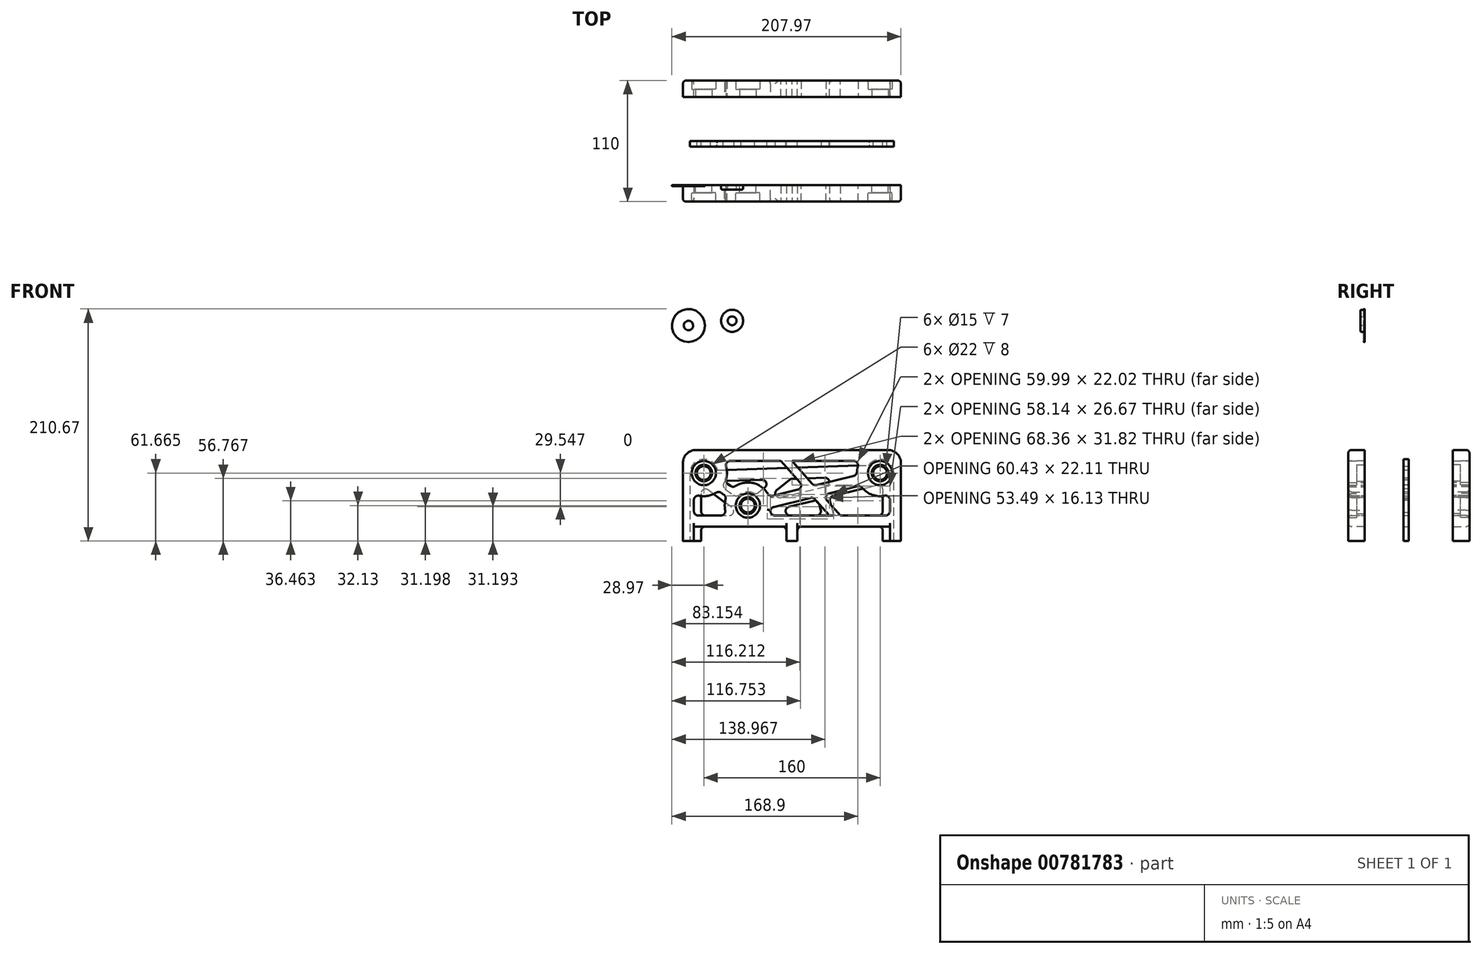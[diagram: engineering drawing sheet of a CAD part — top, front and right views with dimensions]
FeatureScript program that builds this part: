
annotation { "Feature Type Name" : "Feature", "Feature Type Description" : "" }
export const myFeature = defineFeature(function(context is Context, id is Id, definition is map)
    precondition{}
    {
        {
            var Q0;
            Q0=qCreatedBy(makeId("Front.planeOp"),FACE);
            var sketch = newSketch(context, id + "F0", { "sketchPlane" : qUnion([Q0])});
            skCircle(sketch, "E0", {"center": v(0, 0) * mm, "radius": 100 * mm, "construction": true});
            skLineSegment(sketch, "E1", {"start": v(-89.15, -115) * mm, "end": v(130.91, -115) * mm, "construction": true});
            skCircle(sketch, "E2", {"center": v(-80, -66.45) * mm, "radius": 11 * mm});
            skCircle(sketch, "E3", {"center": v(-40, -96) * mm, "radius": 11 * mm});
            skCircle(sketch, "E4", {"center": v(80, -66.45) * mm, "radius": 11 * mm});
            skCircle(sketch, "E5", {"center": v(8.23, -33.43) * mm, "radius": 75 * mm, "construction": true});
            skLineSegment(sketch, "E6", {"start": v(-99, -45.45) * mm, "end": v(-99, -115) * mm});
            skLineSegment(sketch, "E7", {"start": v(-99, -115) * mm, "end": v(99, -115) * mm});
            skLineSegment(sketch, "E8", {"start": v(99, -115) * mm, "end": v(99, -45.45) * mm});
            skCircle(sketch, "E9", {"center": v(-80, -66.45) * mm, "radius": 4 * mm, "construction": true});
            skCircle(sketch, "E10", {"center": v(-40, -96) * mm, "radius": 4 * mm, "construction": true});
            skCircle(sketch, "E11", {"center": v(80, -66.45) * mm, "radius": 4 * mm, "construction": true});
            skLineSegment(sketch, "E12", {"start": v(-99, -45.45) * mm, "end": v(99, -45.45) * mm});
            skCircle(sketch, "E13", {"center": v(-80, -66.45) * mm, "radius": 7.5 * mm});
            skCircle(sketch, "E14", {"center": v(-40, -96) * mm, "radius": 7.5 * mm});
            skCircle(sketch, "E15", {"center": v(80, -66.45) * mm, "radius": 7.5 * mm});
            skSolve(sketch);
        }
        {
            var Q0;
            Q0=makeQuery(id+"F0.imprint","IMPRINT",FACE,{"disambiguationData":[TD([[makeQuery(id+"F0.imprint","IMPRINT",EDGE,{"derivedFrom":sQuery(id+"F0.wireOp",EDGE,"E2")}),-1.0]])]});
            var Q1;
            Q1=makeQuery(id+"F0.imprint","IMPRINT",FACE,{"disambiguationData":[TD([[makeQuery(id+"F0.imprint","IMPRINT",EDGE,{"derivedFrom":sQuery(id+"F0.wireOp",EDGE,"E2")}),1.0]])]});
            var Q2;
            Q2=makeQuery(id+"F0.imprint","IMPRINT",FACE,{"disambiguationData":[TD([[makeQuery(id+"F0.imprint","IMPRINT",EDGE,{"derivedFrom":sQuery(id+"F0.wireOp",EDGE,"E3")}),1.0]])]});
            var Q3;
            Q3=makeQuery(id+"F0.imprint","IMPRINT",FACE,{"disambiguationData":[TD([[makeQuery(id+"F0.imprint","IMPRINT",EDGE,{"derivedFrom":sQuery(id+"F0.wireOp",EDGE,"E4")}),1.0]])]});
            extrude(context, id + "F1", {"entities" : qUnion([Q0, Q1, Q2, Q3]), "depth" : 15 * mm, "offsetDistance" : 25 * mm});
        }
        {
            var Q0;
            Q0=makeQuery(id+"F0.imprint","IMPRINT",FACE,{"disambiguationData":[TD([[makeQuery(id+"F0.imprint","IMPRINT",EDGE,{"derivedFrom":sQuery(id+"F0.wireOp",EDGE,"E2")}),1.0]])]});
            var Q1;
            Q1=makeQuery(id+"F0.imprint","IMPRINT",FACE,{"disambiguationData":[TD([[makeQuery(id+"F0.imprint","IMPRINT",EDGE,{"derivedFrom":sQuery(id+"F0.wireOp",EDGE,"E3")}),1.0]])]});
            var Q2;
            Q2=makeQuery(id+"F0.imprint","IMPRINT",FACE,{"disambiguationData":[TD([[makeQuery(id+"F0.imprint","IMPRINT",EDGE,{"derivedFrom":sQuery(id+"F0.wireOp",EDGE,"E4")}),1.0]])]});
            var Q3;
            Q3=makeQuery(id+"F1.opExtrude","CAP_FACE",FACE,{"disambiguationData":[OSD([sQuery(id+"F0.wireOp",EDGE,"E6"),sQuery(id+"F0.wireOp",EDGE,"E7"),sQuery(id+"F0.wireOp",EDGE,"E8"),sQuery(id+"F0.wireOp",EDGE,"E12"),sQuery(id+"F0.wireOp",EDGE,"E13"),sQuery(id+"F0.wireOp",EDGE,"E14"),sQuery(id+"F0.wireOp",EDGE,"E15")])],"isStart":false});
            extrude(context, id + "F2", {"entities" : qUnion([Q0, Q1, Q2]), "operationType" : NewBodyOperationType.REMOVE, "endBound" : BoundingType.UP_TO_SURFACE, "depth" : 25 * mm, "endBoundEntityFace" : qUnion([Q3]), "offsetDistance" : 25 * mm, "hasSecondDirection" : true, "secondDirectionOppositeDirection" : false, "secondDirectionDepth" : 7 * mm});
        }
        {
            var Q0;
            Q0=makeQuery(id+"F1.opExtrude","CAP_FACE",FACE,{"disambiguationData":[OSD([sQuery(id+"F0.wireOp",EDGE,"E2"),sQuery(id+"F0.wireOp",EDGE,"E3"),sQuery(id+"F0.wireOp",EDGE,"E4"),sQuery(id+"F0.wireOp",EDGE,"E6"),sQuery(id+"F0.wireOp",EDGE,"E7"),sQuery(id+"F0.wireOp",EDGE,"E8"),sQuery(id+"F0.wireOp",EDGE,"md6mKMxj-XIqy-UovL-ZTLQ-MiWI4Y2psHtO"),sQuery(id+"F0.wireOp",EDGE,"icawwdYT-1uhy-4dwY-ULv6-UgLao4UIgMBT"),sQuery(id+"F0.wireOp",EDGE,"7s30I3XL-TyKG-oTAD-cgkG-Kr0AbNeQ8WuT")])],"isStart":false});
            shell(context, id + "F3", {"entities" : qUnion([Q0]), "thickness" : 10 * mm});
        }
        {
            var Q0;
            Q0=makeQuery(id+"F3.opShell","OFFSET_FACE",FACE,{"disambiguationData":[OSD([sQuery(id+"F0.wireOp",EDGE,"E6"),sQuery(id+"F0.wireOp",EDGE,"E7"),sQuery(id+"F0.wireOp",EDGE,"E8"),sQuery(id+"F0.wireOp",EDGE,"E12"),sQuery(id+"F0.wireOp",EDGE,"E13"),sQuery(id+"F0.wireOp",EDGE,"E14"),sQuery(id+"F0.wireOp",EDGE,"E15")])]});
            extrude(context, id + "F4", {"entities" : qUnion([Q0]), "operationType" : NewBodyOperationType.REMOVE, "oppositeDirection" : true, "depth" : 25 * mm, "offsetDistance" : 25 * mm, "symmetric" : true});
        }
        {
            var Q0;
            Q0=makeQuery(id+"F1.opExtrude","CAP_FACE",FACE,{"disambiguationData":[OSD([sQuery(id+"F0.wireOp",EDGE,"E6"),sQuery(id+"F0.wireOp",EDGE,"E7"),sQuery(id+"F0.wireOp",EDGE,"E8"),sQuery(id+"F0.wireOp",EDGE,"E12"),sQuery(id+"F0.wireOp",EDGE,"E13"),sQuery(id+"F0.wireOp",EDGE,"E14"),sQuery(id+"F0.wireOp",EDGE,"E15")])],"isStart":false});
            var sketch = newSketch(context, id + "F5", { "sketchPlane" : qUnion([Q0])});
            skCircle(sketch, "E16.0", {"center": v(-80, -66.45) * mm, "radius": 7.5 * mm, "construction": true});
            skCircle(sketch, "E17.0", {"center": v(-40, -96) * mm, "radius": 7.5 * mm, "construction": true});
            skCircle(sketch, "E18.0", {"center": v(80, -66.45) * mm, "radius": 7.5 * mm, "construction": true});
            skLineSegment(sketch, "E19", {"start": v(-78.47, -73.8) * mm, "end": v(-47.47, -96.7) * mm});
            skLineSegment(sketch, "E20", {"start": v(-81.53, -59.1) * mm, "end": v(-32.53, -95.3) * mm});
            skCircle(sketch, "E21.0", {"center": v(-80, -66.45) * mm, "radius": 11 * mm});
            skCircle(sketch, "E22.0", {"center": v(-40, -96) * mm, "radius": 11 * mm});
            skCircle(sketch, "E23.0", {"center": v(80, -66.45) * mm, "radius": 11 * mm});
            skLineSegment(sketch, "E24", {"start": v(-32.72, -94.2) * mm, "end": v(72.72, -68.25) * mm, "construction": true});
            skLineSegment(sketch, "E25", {"start": v(-30.55, -90.38) * mm, "end": v(69.02, -65.86) * mm});
            skLineSegment(sketch, "E26", {"start": v(73.23, -75.12) * mm, "end": v(-29.98, -100.54) * mm});
            skLineSegment(sketch, "E27", {"start": v(0, -55.45) * mm, "end": v(43.99, -105) * mm});
            skLineSegment(sketch, "E28", {"start": v(33.99, -105) * mm, "end": v(-10, -55.45) * mm});
            skLineSegment(sketch, "E29", {"start": v(-80, -66.45) * mm, "end": v(-40, -96) * mm, "construction": true});
            skSolve(sketch);
        }
        {
            var Q0;
            {var subQ0=sQuery(id+"F5.wireOp",EDGE,"E25");var subQ1=sQuery(id+"F0.wireOp",EDGE,"E15");var subQ2=sQuery(id+"F0.wireOp",EDGE,"E14");var subQ3=sQuery(id+"F0.wireOp",EDGE,"E13");var subQ4=sQuery(id+"F0.wireOp",EDGE,"E12");var subQ5=sQuery(id+"F0.wireOp",EDGE,"E8");var subQ6=sQuery(id+"F0.wireOp",EDGE,"E7");var subQ7=sQuery(id+"F0.wireOp",EDGE,"E6");var subQ8=makeQuery(id+"F3.opShell","OFFSET_EDGE",EDGE,{"disambiguationData":[OSD([sQuery(id+"F0.wireOp",EDGE,"E3"),subQ7,subQ6,subQ5,subQ4,subQ3,subQ2,subQ1])]});var subQ9=makeQuery(id+"F5.imprint","INTERSECT",VERTEX,{"derivedFrom":[subQ8,subQ0]});Q0=makeQuery(id+"F5.imprint","IMPRINT",FACE,{"disambiguationData":[TD([[makeQuery(id+"F5.imprint","IMPRINT",EDGE,{"disambiguationData":[TD([[subQ9,-1.0]])],"derivedFrom":subQ0}),-1.0]])]});}
            var Q1;
            {var subQ0=sQuery(id+"F5.wireOp",EDGE,"E19");var subQ1=sQuery(id+"F0.wireOp",EDGE,"E15");var subQ2=sQuery(id+"F0.wireOp",EDGE,"E14");var subQ3=sQuery(id+"F0.wireOp",EDGE,"E13");var subQ4=sQuery(id+"F0.wireOp",EDGE,"E12");var subQ5=sQuery(id+"F0.wireOp",EDGE,"E8");var subQ6=sQuery(id+"F0.wireOp",EDGE,"E7");var subQ7=sQuery(id+"F0.wireOp",EDGE,"E6");var subQ8=makeQuery(id+"F3.opShell","OFFSET_EDGE",EDGE,{"disambiguationData":[OSD([sQuery(id+"F0.wireOp",EDGE,"E2"),subQ7,subQ6,subQ5,subQ4,subQ3,subQ2,subQ1])]});var subQ9=makeQuery(id+"F5.imprint","INTERSECT",VERTEX,{"derivedFrom":[subQ8,subQ0]});Q1=makeQuery(id+"F5.imprint","IMPRINT",FACE,{"disambiguationData":[TD([[makeQuery(id+"F5.imprint","IMPRINT",EDGE,{"disambiguationData":[TD([[subQ9,-1.0]])],"derivedFrom":subQ0}),1.0]])]});}
            var Q2;
            {var subQ0=sQuery(id+"F5.wireOp",EDGE,"E28");var subQ1=sQuery(id+"F5.wireOp",EDGE,"E25");var subQ2=makeQuery(id+"F5.imprint","INTERSECT",VERTEX,{"derivedFrom":[subQ1,subQ0]});Q2=makeQuery(id+"F5.imprint","IMPRINT",FACE,{"disambiguationData":[TD([[makeQuery(id+"F5.imprint","IMPRINT",EDGE,{"disambiguationData":[TD([[subQ2,-1.0]])],"derivedFrom":subQ1}),1.0]])]});}
            var Q3;
            {var subQ0=sQuery(id+"F5.wireOp",EDGE,"E27");var subQ1=sQuery(id+"F5.wireOp",EDGE,"E25");var subQ2=makeQuery(id+"F5.imprint","INTERSECT",VERTEX,{"derivedFrom":[subQ1,subQ0]});Q3=makeQuery(id+"F5.imprint","IMPRINT",FACE,{"disambiguationData":[TD([[makeQuery(id+"F5.imprint","IMPRINT",EDGE,{"disambiguationData":[TD([[subQ2,-1.0]])],"derivedFrom":subQ0}),1.0]])]});}
            var Q4;
            {var subQ0=sQuery(id+"F5.wireOp",EDGE,"E27");var subQ1=sQuery(id+"F5.wireOp",EDGE,"E26");var subQ2=makeQuery(id+"F5.imprint","INTERSECT",VERTEX,{"derivedFrom":[subQ1,subQ0]});Q4=makeQuery(id+"F5.imprint","IMPRINT",FACE,{"disambiguationData":[TD([[makeQuery(id+"F5.imprint","IMPRINT",EDGE,{"disambiguationData":[TD([[subQ2,-1.0]])],"derivedFrom":subQ1}),1.0]])]});}
            var Q5;
            {var subQ0=sQuery(id+"F5.wireOp",EDGE,"E28");var subQ1=sQuery(id+"F5.wireOp",EDGE,"E25");var subQ2=makeQuery(id+"F5.imprint","INTERSECT",VERTEX,{"derivedFrom":[subQ1,subQ0]});Q5=makeQuery(id+"F5.imprint","IMPRINT",FACE,{"disambiguationData":[TD([[makeQuery(id+"F5.imprint","IMPRINT",EDGE,{"disambiguationData":[TD([[subQ2,-1.0]])],"derivedFrom":subQ1}),-1.0]])]});}
            var Q6;
            Q6=makeQuery(id+"F1.opExtrude","CAP_FACE",FACE,{"disambiguationData":[OSD([sQuery(id+"F0.wireOp",EDGE,"E6"),sQuery(id+"F0.wireOp",EDGE,"E7"),sQuery(id+"F0.wireOp",EDGE,"E8"),sQuery(id+"F0.wireOp",EDGE,"E12"),sQuery(id+"F0.wireOp",EDGE,"E13"),sQuery(id+"F0.wireOp",EDGE,"E14"),sQuery(id+"F0.wireOp",EDGE,"E15")])],"isStart":true});
            extrude(context, id + "F6", {"entities" : qUnion([Q0, Q1, Q2, Q3, Q4, Q5]), "operationType" : NewBodyOperationType.ADD, "endBound" : BoundingType.UP_TO_SURFACE, "oppositeDirection" : true, "depth" : 25 * mm, "endBoundEntityFace" : qUnion([Q6]), "offsetDistance" : 25 * mm});
        }
        {
            var Q0;
            {var subQ0=sQuery(id+"F5.wireOp",EDGE,"E22.0");var subQ1=sQuery(id+"F0.wireOp",EDGE,"E12");var subQ2=sQuery(id+"F0.wireOp",EDGE,"E7");Q0=makeQuery(id+"F6.boolean.opBoolean","MERGE",FACE,{"derivedFrom":[makeQuery(id+"F1.opExtrude","CAP_FACE",FACE,{"disambiguationData":[OSD([sQuery(id+"F0.wireOp",EDGE,"E6"),subQ2,sQuery(id+"F0.wireOp",EDGE,"E8"),subQ1,sQuery(id+"F0.wireOp",EDGE,"E13"),sQuery(id+"F0.wireOp",EDGE,"E14"),sQuery(id+"F0.wireOp",EDGE,"E15")])],"isStart":false}),makeQuery(id+"F6.opExtrude","CAP_FACE",FACE,{"disambiguationData":[OSD([sQuery(id+"F5.wireOp",EDGE,"E19"),sQuery(id+"F5.wireOp",EDGE,"E20"),sQuery(id+"F5.wireOp",EDGE,"E21.0"),subQ0])],"isStart":true}),makeQuery(id+"F6.opExtrude","CAP_FACE",FACE,{"disambiguationData":[OSD([subQ2,subQ1,subQ0,sQuery(id+"F5.wireOp",EDGE,"E23.0"),sQuery(id+"F5.wireOp",EDGE,"E25"),sQuery(id+"F5.wireOp",EDGE,"E26"),sQuery(id+"F5.wireOp",EDGE,"E27"),sQuery(id+"F5.wireOp",EDGE,"E28")])],"isStart":true})]});}
            var sketch = newSketch(context, id + "F7", { "sketchPlane" : qUnion([Q0])});
            skLineSegment(sketch, "E30.bottom", {"start": v(-99, -115) * mm, "end": v(-89, -115) * mm});
            skLineSegment(sketch, "E30.top", {"start": v(-99, -128.13) * mm, "end": v(-89, -128.13) * mm});
            skLineSegment(sketch, "E30.left", {"start": v(-99, -115) * mm, "end": v(-99, -128.13) * mm});
            skLineSegment(sketch, "E30.right", {"start": v(-89, -115) * mm, "end": v(-89, -128.13) * mm});
            skLineSegment(sketch, "E31.bottom", {"start": v(99, -115) * mm, "end": v(89, -115) * mm});
            skLineSegment(sketch, "E31.top", {"start": v(99, -128.13) * mm, "end": v(89, -128.13) * mm});
            skLineSegment(sketch, "E31.left", {"start": v(99, -115) * mm, "end": v(99, -128.13) * mm});
            skLineSegment(sketch, "E31.right", {"start": v(89, -115) * mm, "end": v(89, -128.13) * mm});
            skLineSegment(sketch, "E32", {"start": v(0, -115) * mm, "end": v(0, -129) * mm, "construction": true});
            skLineSegment(sketch, "E33.bottom", {"start": v(-5, -115) * mm, "end": v(5, -115) * mm});
            skLineSegment(sketch, "E33.top", {"start": v(-5, -128.13) * mm, "end": v(5, -128.13) * mm});
            skLineSegment(sketch, "E33.left", {"start": v(-5, -115) * mm, "end": v(-5, -128.13) * mm});
            skLineSegment(sketch, "E33.right", {"start": v(5, -115) * mm, "end": v(5, -128.13) * mm});
            skSolve(sketch);
        }
        {
            var Q0;
            Q0=makeQuery(id+"F7.imprint","IMPRINT",FACE,{"disambiguationData":[TD([[makeQuery(id+"F7.imprint","IMPRINT",EDGE,{"derivedFrom":sQuery(id+"F7.wireOp",EDGE,"E30.bottom")}),-1.0]])]});
            var Q1;
            Q1=makeQuery(id+"F7.imprint","IMPRINT",FACE,{"disambiguationData":[TD([[makeQuery(id+"F7.imprint","IMPRINT",EDGE,{"derivedFrom":sQuery(id+"F7.wireOp",EDGE,"E33.bottom")}),-1.0]])]});
            var Q2;
            Q2=makeQuery(id+"F7.imprint","IMPRINT",FACE,{"disambiguationData":[TD([[makeQuery(id+"F7.imprint","IMPRINT",EDGE,{"derivedFrom":sQuery(id+"F7.wireOp",EDGE,"E31.bottom")}),-1.0]])]});
            var Q3;
            {var subQ0=sQuery(id+"F5.wireOp",EDGE,"E22.0");var subQ1=sQuery(id+"F0.wireOp",EDGE,"E12");var subQ2=sQuery(id+"F0.wireOp",EDGE,"E7");Q3=makeQuery(id+"F6.boolean.opBoolean","MERGE",FACE,{"derivedFrom":[makeQuery(id+"F1.opExtrude","CAP_FACE",FACE,{"disambiguationData":[OSD([sQuery(id+"F0.wireOp",EDGE,"E6"),subQ2,sQuery(id+"F0.wireOp",EDGE,"E8"),subQ1,sQuery(id+"F0.wireOp",EDGE,"E13"),sQuery(id+"F0.wireOp",EDGE,"E14"),sQuery(id+"F0.wireOp",EDGE,"E15")])],"isStart":true}),makeQuery(id+"F6.opExtrude","CAP_FACE",FACE,{"disambiguationData":[OSD([sQuery(id+"F5.wireOp",EDGE,"E19"),sQuery(id+"F5.wireOp",EDGE,"E20"),sQuery(id+"F5.wireOp",EDGE,"E21.0"),subQ0])],"isStart":false}),makeQuery(id+"F6.opExtrude","CAP_FACE",FACE,{"disambiguationData":[OSD([subQ2,subQ1,subQ0,sQuery(id+"F5.wireOp",EDGE,"E23.0"),sQuery(id+"F5.wireOp",EDGE,"E25"),sQuery(id+"F5.wireOp",EDGE,"E26"),sQuery(id+"F5.wireOp",EDGE,"E27"),sQuery(id+"F5.wireOp",EDGE,"E28")])],"isStart":false})]});}
            extrude(context, id + "F8", {"entities" : qUnion([Q0, Q1, Q2]), "operationType" : NewBodyOperationType.ADD, "endBound" : BoundingType.UP_TO_SURFACE, "oppositeDirection" : true, "depth" : 25 * mm, "endBoundEntityFace" : qUnion([Q3]), "offsetDistance" : 25 * mm});
        }
        {
            var Q0;
            Q0=makeQuery(id+"F1.opExtrude","SWEPT_EDGE",EDGE,{"disambiguationData":[OSD([sQuery(id+"F0.wireOp",EDGE,"E6"),sQuery(id+"F0.wireOp",EDGE,"E12")])]});
            var Q1;
            Q1=makeQuery(id+"F1.opExtrude","SWEPT_EDGE",EDGE,{"disambiguationData":[OSD([sQuery(id+"F0.wireOp",EDGE,"E8"),sQuery(id+"F0.wireOp",EDGE,"E12")])]});
            fillet(context, id + "F9", {"entities" : qUnion([Q0, Q1]), "radius" : 12 * mm, "tangentPropagation" : true, "allowEdgeOverflow" : false});
        }
        {
            var Q0;
            {var subQ0=sQuery(id+"F0.wireOp",EDGE,"E2");var subQ1=makeQuery(id+"F2.boolean.opBoolean","COPY",FACE,{"derivedFrom":makeQuery(id+"F2.opExtrude","SWEPT_FACE",FACE,{"disambiguationData":[OSD([subQ0])]})});var subQ2=sQuery(id+"F0.wireOp",EDGE,"E12");var subQ3=makeQuery(id+"F1.opExtrude","SWEPT_FACE",FACE,{"disambiguationData":[OSD([subQ2])]});var subQ4=sQuery(id+"F0.wireOp",EDGE,"E15");var subQ5=sQuery(id+"F0.wireOp",EDGE,"E14");var subQ6=sQuery(id+"F0.wireOp",EDGE,"E13");var subQ7=sQuery(id+"F0.wireOp",EDGE,"E8");var subQ8=sQuery(id+"F0.wireOp",EDGE,"E7");var subQ9=sQuery(id+"F0.wireOp",EDGE,"E6");Q0=makeQuery(id+"F4.boolean.opBoolean","MERGE",EDGE,{"derivedFrom":[makeQuery(id+"F3.opShell","TWEAK_EDGE",EDGE,{"derivedFrom":[subQ3,subQ1]})],"fromTools":[makeQuery(id+"F4.opExtrude","SWEPT_EDGE",EDGE,{"disambiguationData":[OSD([subQ0,subQ9,subQ8,subQ7,subQ2,subQ6,subQ5,subQ4]),TDD([makeQuery(id+"F3.opShell","TWEAK_VERTEX",VERTEX,{"derivedFrom":[makeQuery(id+"F1.opExtrude","CAP_FACE",FACE,{"disambiguationData":[OSD([subQ9,subQ8,subQ7,subQ2,subQ6,subQ5,subQ4])],"isStart":true}),subQ3,subQ1]})])]})]});}
            var Q1;
            Q1=makeQuery(id+"F6.opExtrude","SWEPT_EDGE",EDGE,{"disambiguationData":[OSD([sQuery(id+"F0.wireOp",EDGE,"E12"),sQuery(id+"F5.wireOp",EDGE,"E28")])]});
            var Q2;
            Q2=makeQuery(id+"F6.opExtrude","SWEPT_EDGE",EDGE,{"disambiguationData":[OSD([sQuery(id+"F0.wireOp",EDGE,"E12"),sQuery(id+"F5.wireOp",EDGE,"E27")])]});
            var Q3;
            {var subQ0=sQuery(id+"F0.wireOp",EDGE,"E4");var subQ1=makeQuery(id+"F2.boolean.opBoolean","COPY",FACE,{"derivedFrom":makeQuery(id+"F2.opExtrude","SWEPT_FACE",FACE,{"disambiguationData":[OSD([subQ0])]})});var subQ2=sQuery(id+"F0.wireOp",EDGE,"E12");var subQ3=makeQuery(id+"F1.opExtrude","SWEPT_FACE",FACE,{"disambiguationData":[OSD([subQ2])]});var subQ4=sQuery(id+"F0.wireOp",EDGE,"E15");var subQ5=sQuery(id+"F0.wireOp",EDGE,"E14");var subQ6=sQuery(id+"F0.wireOp",EDGE,"E13");var subQ7=sQuery(id+"F0.wireOp",EDGE,"E8");var subQ8=sQuery(id+"F0.wireOp",EDGE,"E7");var subQ9=sQuery(id+"F0.wireOp",EDGE,"E6");Q3=makeQuery(id+"F4.boolean.opBoolean","MERGE",EDGE,{"derivedFrom":[makeQuery(id+"F3.opShell","TWEAK_EDGE",EDGE,{"derivedFrom":[subQ3,subQ1]})],"fromTools":[makeQuery(id+"F4.opExtrude","SWEPT_EDGE",EDGE,{"disambiguationData":[OSD([subQ0,subQ9,subQ8,subQ7,subQ2,subQ6,subQ5,subQ4]),TDD([makeQuery(id+"F3.opShell","TWEAK_VERTEX",VERTEX,{"derivedFrom":[makeQuery(id+"F1.opExtrude","CAP_FACE",FACE,{"disambiguationData":[OSD([subQ9,subQ8,subQ7,subQ2,subQ6,subQ5,subQ4])],"isStart":true}),subQ3,subQ1]})])]})]});}
            var Q4;
            {var subQ0=sQuery(id+"F5.wireOp",EDGE,"E25");var subQ1=sQuery(id+"F0.wireOp",EDGE,"E4");Q4=makeQuery(id+"F6.boolean.opBoolean","INTERSECT",EDGE,{"derivedFrom":[makeQuery(id+"F4.boolean.opBoolean","MERGE",FACE,{"derivedFrom":[makeQuery(id+"F3.opShell","OFFSET_FACE",FACE,{"disambiguationData":[OSD([subQ1])]})],"fromTools":[makeQuery(id+"F4.opExtrude","SWEPT_FACE",FACE,{"disambiguationData":[OSD([subQ1,sQuery(id+"F0.wireOp",EDGE,"E6"),sQuery(id+"F0.wireOp",EDGE,"E7"),sQuery(id+"F0.wireOp",EDGE,"E8"),sQuery(id+"F0.wireOp",EDGE,"E12"),sQuery(id+"F0.wireOp",EDGE,"E13"),sQuery(id+"F0.wireOp",EDGE,"E14"),sQuery(id+"F0.wireOp",EDGE,"E15")])]})]}),makeQuery(id+"F6.opExtrude","SWEPT_FACE",FACE,{"disambiguationData":[OSD([subQ0]),TDD([makeQuery(id+"F5.imprint","IMPRINT",EDGE,{"disambiguationData":[TD([[makeQuery(id+"F5.imprint","INTERSECT",VERTEX,{"derivedFrom":[subQ0,sQuery(id+"F5.wireOp",EDGE,"E27")]}),-1.0]])],"derivedFrom":subQ0}),makeQuery(id+"F5.imprint","IMPRINT",EDGE,{"disambiguationData":[TD([[makeQuery(id+"F5.imprint","INTERSECT",VERTEX,{"derivedFrom":[sQuery(id+"F5.wireOp",EDGE,"E23.0"),subQ0]}),1.0]])],"derivedFrom":subQ0})])]})]});}
            var Q5;
            Q5=makeQuery(id+"F6.opExtrude","SWEPT_EDGE",EDGE,{"disambiguationData":[OSD([sQuery(id+"F5.wireOp",EDGE,"E25"),sQuery(id+"F5.wireOp",EDGE,"E27")])]});
            var Q6;
            Q6=makeQuery(id+"F6.opExtrude","SWEPT_EDGE",EDGE,{"disambiguationData":[OSD([sQuery(id+"F5.wireOp",EDGE,"E25"),sQuery(id+"F5.wireOp",EDGE,"E28")])]});
            var Q7;
            {var subQ0=sQuery(id+"F5.wireOp",EDGE,"E25");var subQ1=sQuery(id+"F0.wireOp",EDGE,"E3");Q7=makeQuery(id+"F6.boolean.opBoolean","INTERSECT",EDGE,{"derivedFrom":[makeQuery(id+"F4.boolean.opBoolean","MERGE",FACE,{"derivedFrom":[makeQuery(id+"F3.opShell","OFFSET_FACE",FACE,{"disambiguationData":[OSD([subQ1])]})],"fromTools":[makeQuery(id+"F4.opExtrude","SWEPT_FACE",FACE,{"disambiguationData":[OSD([subQ1,sQuery(id+"F0.wireOp",EDGE,"E6"),sQuery(id+"F0.wireOp",EDGE,"E7"),sQuery(id+"F0.wireOp",EDGE,"E8"),sQuery(id+"F0.wireOp",EDGE,"E12"),sQuery(id+"F0.wireOp",EDGE,"E13"),sQuery(id+"F0.wireOp",EDGE,"E14"),sQuery(id+"F0.wireOp",EDGE,"E15")])]})]}),makeQuery(id+"F6.opExtrude","SWEPT_FACE",FACE,{"disambiguationData":[OSD([subQ0]),TDD([makeQuery(id+"F5.imprint","IMPRINT",EDGE,{"disambiguationData":[TD([[makeQuery(id+"F5.imprint","INTERSECT",VERTEX,{"derivedFrom":[sQuery(id+"F5.wireOp",EDGE,"E22.0"),subQ0]}),-1.0]])],"derivedFrom":subQ0}),makeQuery(id+"F5.imprint","IMPRINT",EDGE,{"disambiguationData":[TD([[makeQuery(id+"F5.imprint","INTERSECT",VERTEX,{"derivedFrom":[subQ0,sQuery(id+"F5.wireOp",EDGE,"E28")]}),1.0]])],"derivedFrom":subQ0})])]})]});}
            var Q8;
            {var subQ0=sQuery(id+"F0.wireOp",EDGE,"E3");Q8=makeQuery(id+"F6.boolean.opBoolean","INTERSECT",EDGE,{"derivedFrom":[makeQuery(id+"F4.boolean.opBoolean","MERGE",FACE,{"derivedFrom":[makeQuery(id+"F3.opShell","OFFSET_FACE",FACE,{"disambiguationData":[OSD([subQ0])]})],"fromTools":[makeQuery(id+"F4.opExtrude","SWEPT_FACE",FACE,{"disambiguationData":[OSD([subQ0,sQuery(id+"F0.wireOp",EDGE,"E6"),sQuery(id+"F0.wireOp",EDGE,"E7"),sQuery(id+"F0.wireOp",EDGE,"E8"),sQuery(id+"F0.wireOp",EDGE,"E12"),sQuery(id+"F0.wireOp",EDGE,"E13"),sQuery(id+"F0.wireOp",EDGE,"E14"),sQuery(id+"F0.wireOp",EDGE,"E15")])]})]}),makeQuery(id+"F6.opExtrude","SWEPT_FACE",FACE,{"disambiguationData":[OSD([sQuery(id+"F5.wireOp",EDGE,"E20")])]})]});}
            var Q9;
            {var subQ0=sQuery(id+"F0.wireOp",EDGE,"E2");Q9=makeQuery(id+"F6.boolean.opBoolean","INTERSECT",EDGE,{"derivedFrom":[makeQuery(id+"F4.boolean.opBoolean","MERGE",FACE,{"derivedFrom":[makeQuery(id+"F3.opShell","OFFSET_FACE",FACE,{"disambiguationData":[OSD([subQ0])]})],"fromTools":[makeQuery(id+"F4.opExtrude","SWEPT_FACE",FACE,{"disambiguationData":[OSD([subQ0,sQuery(id+"F0.wireOp",EDGE,"E6"),sQuery(id+"F0.wireOp",EDGE,"E7"),sQuery(id+"F0.wireOp",EDGE,"E8"),sQuery(id+"F0.wireOp",EDGE,"E12"),sQuery(id+"F0.wireOp",EDGE,"E13"),sQuery(id+"F0.wireOp",EDGE,"E14"),sQuery(id+"F0.wireOp",EDGE,"E15")])]})]}),makeQuery(id+"F6.opExtrude","SWEPT_FACE",FACE,{"disambiguationData":[OSD([sQuery(id+"F5.wireOp",EDGE,"E20")])]})]});}
            var Q10;
            {var subQ0=sQuery(id+"F0.wireOp",EDGE,"E2");Q10=makeQuery(id+"F6.boolean.opBoolean","INTERSECT",EDGE,{"derivedFrom":[makeQuery(id+"F4.boolean.opBoolean","MERGE",FACE,{"derivedFrom":[makeQuery(id+"F3.opShell","OFFSET_FACE",FACE,{"disambiguationData":[OSD([subQ0])]})],"fromTools":[makeQuery(id+"F4.opExtrude","SWEPT_FACE",FACE,{"disambiguationData":[OSD([subQ0,sQuery(id+"F0.wireOp",EDGE,"E6"),sQuery(id+"F0.wireOp",EDGE,"E7"),sQuery(id+"F0.wireOp",EDGE,"E8"),sQuery(id+"F0.wireOp",EDGE,"E12"),sQuery(id+"F0.wireOp",EDGE,"E13"),sQuery(id+"F0.wireOp",EDGE,"E14"),sQuery(id+"F0.wireOp",EDGE,"E15")])]})]}),makeQuery(id+"F6.opExtrude","SWEPT_FACE",FACE,{"disambiguationData":[OSD([sQuery(id+"F5.wireOp",EDGE,"E19")])]})]});}
            var Q11;
            {var subQ0=sQuery(id+"F0.wireOp",EDGE,"E3");Q11=makeQuery(id+"F6.boolean.opBoolean","INTERSECT",EDGE,{"derivedFrom":[makeQuery(id+"F4.boolean.opBoolean","MERGE",FACE,{"derivedFrom":[makeQuery(id+"F3.opShell","OFFSET_FACE",FACE,{"disambiguationData":[OSD([subQ0])]})],"fromTools":[makeQuery(id+"F4.opExtrude","SWEPT_FACE",FACE,{"disambiguationData":[OSD([subQ0,sQuery(id+"F0.wireOp",EDGE,"E6"),sQuery(id+"F0.wireOp",EDGE,"E7"),sQuery(id+"F0.wireOp",EDGE,"E8"),sQuery(id+"F0.wireOp",EDGE,"E12"),sQuery(id+"F0.wireOp",EDGE,"E13"),sQuery(id+"F0.wireOp",EDGE,"E14"),sQuery(id+"F0.wireOp",EDGE,"E15")])]})]}),makeQuery(id+"F6.opExtrude","SWEPT_FACE",FACE,{"disambiguationData":[OSD([sQuery(id+"F5.wireOp",EDGE,"E19")])]})]});}
            var Q12;
            {var subQ0=sQuery(id+"F0.wireOp",EDGE,"E2");var subQ1=makeQuery(id+"F2.boolean.opBoolean","COPY",FACE,{"derivedFrom":makeQuery(id+"F2.opExtrude","SWEPT_FACE",FACE,{"disambiguationData":[OSD([subQ0])]})});var subQ2=sQuery(id+"F0.wireOp",EDGE,"E15");var subQ3=sQuery(id+"F0.wireOp",EDGE,"E14");var subQ4=sQuery(id+"F0.wireOp",EDGE,"E13");var subQ5=sQuery(id+"F0.wireOp",EDGE,"E12");var subQ6=sQuery(id+"F0.wireOp",EDGE,"E8");var subQ7=sQuery(id+"F0.wireOp",EDGE,"E7");var subQ8=sQuery(id+"F0.wireOp",EDGE,"E6");var subQ9=makeQuery(id+"F1.opExtrude","SWEPT_FACE",FACE,{"disambiguationData":[OSD([subQ8])]});Q12=makeQuery(id+"F4.boolean.opBoolean","MERGE",EDGE,{"derivedFrom":[makeQuery(id+"F3.opShell","TWEAK_EDGE",EDGE,{"derivedFrom":[subQ9,subQ1]})],"fromTools":[makeQuery(id+"F4.opExtrude","SWEPT_EDGE",EDGE,{"disambiguationData":[OSD([subQ0,subQ8,subQ7,subQ6,subQ5,subQ4,subQ3,subQ2]),TDD([makeQuery(id+"F3.opShell","TWEAK_VERTEX",VERTEX,{"derivedFrom":[subQ9,makeQuery(id+"F1.opExtrude","CAP_FACE",FACE,{"disambiguationData":[OSD([subQ8,subQ7,subQ6,subQ5,subQ4,subQ3,subQ2])],"isStart":true}),subQ1]})])]})]});}
            var Q13;
            {var subQ0=sQuery(id+"F0.wireOp",EDGE,"E7");var subQ1=sQuery(id+"F0.wireOp",EDGE,"E6");Q13=makeQuery(id+"F4.boolean.opBoolean","MERGE",EDGE,{"derivedFrom":[makeQuery(id+"F3.opShell","OFFSET_EDGE",EDGE,{"disambiguationData":[OSD([subQ1,subQ0])]}),makeQuery(id+"F4.opExtrude","SWEPT_EDGE",EDGE,{"disambiguationData":[OSD([subQ1,subQ0])]})]});}
            var Q14;
            {var subQ0=sQuery(id+"F0.wireOp",EDGE,"E3");var subQ1=makeQuery(id+"F2.boolean.opBoolean","COPY",FACE,{"derivedFrom":makeQuery(id+"F2.opExtrude","SWEPT_FACE",FACE,{"disambiguationData":[OSD([subQ0])]})});var subQ2=sQuery(id+"F0.wireOp",EDGE,"E7");var subQ3=makeQuery(id+"F1.opExtrude","SWEPT_FACE",FACE,{"disambiguationData":[OSD([subQ2])]});var subQ4=sQuery(id+"F0.wireOp",EDGE,"E15");var subQ5=sQuery(id+"F0.wireOp",EDGE,"E14");var subQ6=sQuery(id+"F0.wireOp",EDGE,"E13");var subQ7=sQuery(id+"F0.wireOp",EDGE,"E12");var subQ8=sQuery(id+"F0.wireOp",EDGE,"E8");var subQ9=sQuery(id+"F0.wireOp",EDGE,"E6");Q14=makeQuery(id+"F4.boolean.opBoolean","MERGE",EDGE,{"derivedFrom":[makeQuery(id+"F3.opShell","TWEAK_EDGE",EDGE,{"disambiguationData":[OD(0.0)],"derivedFrom":[subQ3,subQ1]})],"fromTools":[makeQuery(id+"F4.opExtrude","SWEPT_EDGE",EDGE,{"disambiguationData":[OSD([subQ0,subQ9,subQ2,subQ8,subQ7,subQ6,subQ5,subQ4]),TDD([makeQuery(id+"F3.opShell","TWEAK_VERTEX",VERTEX,{"disambiguationData":[OD(0.0)],"derivedFrom":[makeQuery(id+"F1.opExtrude","CAP_FACE",FACE,{"disambiguationData":[OSD([subQ9,subQ2,subQ8,subQ7,subQ6,subQ5,subQ4])],"isStart":true}),subQ3,subQ1]})])]})]});}
            var Q15;
            {var subQ0=sQuery(id+"F5.wireOp",EDGE,"E26");var subQ1=sQuery(id+"F0.wireOp",EDGE,"E3");Q15=makeQuery(id+"F6.boolean.opBoolean","INTERSECT",EDGE,{"derivedFrom":[makeQuery(id+"F4.boolean.opBoolean","MERGE",FACE,{"derivedFrom":[makeQuery(id+"F3.opShell","OFFSET_FACE",FACE,{"disambiguationData":[OSD([subQ1])]})],"fromTools":[makeQuery(id+"F4.opExtrude","SWEPT_FACE",FACE,{"disambiguationData":[OSD([subQ1,sQuery(id+"F0.wireOp",EDGE,"E6"),sQuery(id+"F0.wireOp",EDGE,"E7"),sQuery(id+"F0.wireOp",EDGE,"E8"),sQuery(id+"F0.wireOp",EDGE,"E12"),sQuery(id+"F0.wireOp",EDGE,"E13"),sQuery(id+"F0.wireOp",EDGE,"E14"),sQuery(id+"F0.wireOp",EDGE,"E15")])]})]}),makeQuery(id+"F6.opExtrude","SWEPT_FACE",FACE,{"disambiguationData":[OSD([subQ0]),TDD([makeQuery(id+"F5.imprint","IMPRINT",EDGE,{"disambiguationData":[TD([[makeQuery(id+"F5.imprint","INTERSECT",VERTEX,{"derivedFrom":[subQ0,sQuery(id+"F5.wireOp",EDGE,"E28")]}),-1.0]])],"derivedFrom":subQ0}),makeQuery(id+"F5.imprint","IMPRINT",EDGE,{"disambiguationData":[TD([[makeQuery(id+"F5.imprint","INTERSECT",VERTEX,{"derivedFrom":[sQuery(id+"F5.wireOp",EDGE,"E22.0"),subQ0]}),1.0]])],"derivedFrom":subQ0})])]})]});}
            var Q16;
            {var subQ0=sQuery(id+"F0.wireOp",EDGE,"E3");var subQ1=makeQuery(id+"F2.boolean.opBoolean","COPY",FACE,{"derivedFrom":makeQuery(id+"F2.opExtrude","SWEPT_FACE",FACE,{"disambiguationData":[OSD([subQ0])]})});var subQ2=sQuery(id+"F0.wireOp",EDGE,"E7");var subQ3=makeQuery(id+"F1.opExtrude","SWEPT_FACE",FACE,{"disambiguationData":[OSD([subQ2])]});var subQ4=sQuery(id+"F0.wireOp",EDGE,"E15");var subQ5=sQuery(id+"F0.wireOp",EDGE,"E14");var subQ6=sQuery(id+"F0.wireOp",EDGE,"E13");var subQ7=sQuery(id+"F0.wireOp",EDGE,"E12");var subQ8=sQuery(id+"F0.wireOp",EDGE,"E8");var subQ9=sQuery(id+"F0.wireOp",EDGE,"E6");Q16=makeQuery(id+"F4.boolean.opBoolean","MERGE",EDGE,{"derivedFrom":[makeQuery(id+"F3.opShell","TWEAK_EDGE",EDGE,{"disambiguationData":[OD(1.0)],"derivedFrom":[subQ3,subQ1]})],"fromTools":[makeQuery(id+"F4.opExtrude","SWEPT_EDGE",EDGE,{"disambiguationData":[OSD([subQ0,subQ9,subQ2,subQ8,subQ7,subQ6,subQ5,subQ4]),TDD([makeQuery(id+"F3.opShell","TWEAK_VERTEX",VERTEX,{"disambiguationData":[OD(1.0)],"derivedFrom":[makeQuery(id+"F1.opExtrude","CAP_FACE",FACE,{"disambiguationData":[OSD([subQ9,subQ2,subQ8,subQ7,subQ6,subQ5,subQ4])],"isStart":true}),subQ3,subQ1]})])]})]});}
            var Q17;
            Q17=makeQuery(id+"F6.opExtrude","SWEPT_EDGE",EDGE,{"disambiguationData":[OSD([sQuery(id+"F5.wireOp",EDGE,"E26"),sQuery(id+"F5.wireOp",EDGE,"E28")])]});
            var Q18;
            Q18=makeQuery(id+"F6.opExtrude","SWEPT_EDGE",EDGE,{"disambiguationData":[OSD([sQuery(id+"F0.wireOp",EDGE,"E7"),sQuery(id+"F5.wireOp",EDGE,"E28")])]});
            var Q19;
            Q19=makeQuery(id+"F6.opExtrude","SWEPT_EDGE",EDGE,{"disambiguationData":[OSD([sQuery(id+"F5.wireOp",EDGE,"E26"),sQuery(id+"F5.wireOp",EDGE,"E27")])]});
            var Q20;
            Q20=makeQuery(id+"F6.opExtrude","SWEPT_EDGE",EDGE,{"disambiguationData":[OSD([sQuery(id+"F0.wireOp",EDGE,"E7"),sQuery(id+"F5.wireOp",EDGE,"E27")])]});
            var Q21;
            {var subQ0=sQuery(id+"F0.wireOp",EDGE,"E8");var subQ1=sQuery(id+"F0.wireOp",EDGE,"E7");Q21=makeQuery(id+"F4.boolean.opBoolean","MERGE",EDGE,{"derivedFrom":[makeQuery(id+"F3.opShell","OFFSET_EDGE",EDGE,{"disambiguationData":[OSD([subQ1,subQ0])]}),makeQuery(id+"F4.opExtrude","SWEPT_EDGE",EDGE,{"disambiguationData":[OSD([subQ1,subQ0])]})]});}
            var Q22;
            {var subQ0=sQuery(id+"F0.wireOp",EDGE,"E4");var subQ1=makeQuery(id+"F2.boolean.opBoolean","COPY",FACE,{"derivedFrom":makeQuery(id+"F2.opExtrude","SWEPT_FACE",FACE,{"disambiguationData":[OSD([subQ0])]})});var subQ2=sQuery(id+"F0.wireOp",EDGE,"E8");var subQ3=makeQuery(id+"F1.opExtrude","SWEPT_FACE",FACE,{"disambiguationData":[OSD([subQ2])]});var subQ4=sQuery(id+"F0.wireOp",EDGE,"E15");var subQ5=sQuery(id+"F0.wireOp",EDGE,"E14");var subQ6=sQuery(id+"F0.wireOp",EDGE,"E13");var subQ7=sQuery(id+"F0.wireOp",EDGE,"E12");var subQ8=sQuery(id+"F0.wireOp",EDGE,"E7");var subQ9=sQuery(id+"F0.wireOp",EDGE,"E6");Q22=makeQuery(id+"F4.boolean.opBoolean","MERGE",EDGE,{"derivedFrom":[makeQuery(id+"F3.opShell","TWEAK_EDGE",EDGE,{"derivedFrom":[subQ3,subQ1]})],"fromTools":[makeQuery(id+"F4.opExtrude","SWEPT_EDGE",EDGE,{"disambiguationData":[OSD([subQ0,subQ9,subQ8,subQ2,subQ7,subQ6,subQ5,subQ4]),TDD([makeQuery(id+"F3.opShell","TWEAK_VERTEX",VERTEX,{"derivedFrom":[makeQuery(id+"F1.opExtrude","CAP_FACE",FACE,{"disambiguationData":[OSD([subQ9,subQ8,subQ2,subQ7,subQ6,subQ5,subQ4])],"isStart":true}),subQ3,subQ1]})])]})]});}
            var Q23;
            {var subQ0=sQuery(id+"F5.wireOp",EDGE,"E26");var subQ1=sQuery(id+"F0.wireOp",EDGE,"E4");Q23=makeQuery(id+"F6.boolean.opBoolean","INTERSECT",EDGE,{"derivedFrom":[makeQuery(id+"F4.boolean.opBoolean","MERGE",FACE,{"derivedFrom":[makeQuery(id+"F3.opShell","OFFSET_FACE",FACE,{"disambiguationData":[OSD([subQ1])]})],"fromTools":[makeQuery(id+"F4.opExtrude","SWEPT_FACE",FACE,{"disambiguationData":[OSD([subQ1,sQuery(id+"F0.wireOp",EDGE,"E6"),sQuery(id+"F0.wireOp",EDGE,"E7"),sQuery(id+"F0.wireOp",EDGE,"E8"),sQuery(id+"F0.wireOp",EDGE,"E12"),sQuery(id+"F0.wireOp",EDGE,"E13"),sQuery(id+"F0.wireOp",EDGE,"E14"),sQuery(id+"F0.wireOp",EDGE,"E15")])]})]}),makeQuery(id+"F6.opExtrude","SWEPT_FACE",FACE,{"disambiguationData":[OSD([subQ0]),TDD([makeQuery(id+"F5.imprint","IMPRINT",EDGE,{"disambiguationData":[TD([[makeQuery(id+"F5.imprint","INTERSECT",VERTEX,{"derivedFrom":[sQuery(id+"F5.wireOp",EDGE,"E23.0"),subQ0]}),-1.0]])],"derivedFrom":subQ0}),makeQuery(id+"F5.imprint","IMPRINT",EDGE,{"disambiguationData":[TD([[makeQuery(id+"F5.imprint","INTERSECT",VERTEX,{"derivedFrom":[subQ0,sQuery(id+"F5.wireOp",EDGE,"E27")]}),1.0]])],"derivedFrom":subQ0})])]})]});}
            var Q24;
            Q24=makeQuery(id+"F8.opExtrude","SWEPT_EDGE",EDGE,{"disambiguationData":[OSD([sQuery(id+"F0.wireOp",EDGE,"E7"),sQuery(id+"F7.wireOp",EDGE,"E30.bottom"),sQuery(id+"F7.wireOp",EDGE,"E30.right")])]});
            var Q25;
            Q25=makeQuery(id+"F8.opExtrude","SWEPT_EDGE",EDGE,{"disambiguationData":[OSD([sQuery(id+"F0.wireOp",EDGE,"E7"),sQuery(id+"F7.wireOp",EDGE,"E33.bottom"),sQuery(id+"F7.wireOp",EDGE,"E33.right")])]});
            var Q26;
            Q26=makeQuery(id+"F8.opExtrude","SWEPT_EDGE",EDGE,{"disambiguationData":[OSD([sQuery(id+"F0.wireOp",EDGE,"E7"),sQuery(id+"F7.wireOp",EDGE,"E33.bottom"),sQuery(id+"F7.wireOp",EDGE,"E33.left")])]});
            var Q27;
            Q27=makeQuery(id+"F8.opExtrude","SWEPT_EDGE",EDGE,{"disambiguationData":[OSD([sQuery(id+"F0.wireOp",EDGE,"E7"),sQuery(id+"F7.wireOp",EDGE,"E31.bottom"),sQuery(id+"F7.wireOp",EDGE,"E31.right")])]});
            fillet(context, id + "F10", {"entities" : qUnion([Q0, Q1, Q2, Q3, Q4, Q5, Q6, Q7, Q8, Q9, Q10, Q11, Q12, Q13, Q14, Q15, Q16, Q17, Q18, Q19, Q20, Q21, Q22, Q23, Q24, Q25, Q26, Q27]), "radius" : 4 * mm, "tangentPropagation" : true, "allowEdgeOverflow" : false});
        }
        {
            var Q0;
            Q0=makeQuery(id+"F2.boolean.opBoolean","COPY",EDGE,{"derivedFrom":makeQuery(id+"F2.opExtrude","CAP_EDGE",EDGE,{"disambiguationData":[OSD([sQuery(id+"F0.wireOp",EDGE,"E2")])],"isStart":false})});
            var Q1;
            {var subQ0=sQuery(id+"F5.wireOp",EDGE,"E22.0");var subQ1=sQuery(id+"F0.wireOp",EDGE,"E12");var subQ2=sQuery(id+"F0.wireOp",EDGE,"E7");var subQ3=sQuery(id+"F5.wireOp",EDGE,"E19");var subQ4=sQuery(id+"F0.wireOp",EDGE,"E15");var subQ5=sQuery(id+"F0.wireOp",EDGE,"E14");var subQ6=sQuery(id+"F0.wireOp",EDGE,"E13");var subQ7=sQuery(id+"F0.wireOp",EDGE,"E8");var subQ8=sQuery(id+"F0.wireOp",EDGE,"E6");var subQ9=sQuery(id+"F0.wireOp",EDGE,"E2");Q1=makeQuery(id+"F10.opFillet","BLEND_EDGE",EDGE,{"blendedFrom":[makeQuery(id+"F6.boolean.opBoolean","INTERSECT",EDGE,{"derivedFrom":[makeQuery(id+"F4.boolean.opBoolean","MERGE",FACE,{"derivedFrom":[makeQuery(id+"F3.opShell","OFFSET_FACE",FACE,{"disambiguationData":[OSD([subQ9])]})],"fromTools":[makeQuery(id+"F4.opExtrude","SWEPT_FACE",FACE,{"disambiguationData":[OSD([subQ9,subQ8,subQ2,subQ7,subQ1,subQ6,subQ5,subQ4])]})]}),makeQuery(id+"F6.opExtrude","SWEPT_FACE",FACE,{"disambiguationData":[OSD([subQ3])]})]}),makeQuery(id+"F8.boolean.opBoolean","MERGE",FACE,{"derivedFrom":[makeQuery(id+"F6.boolean.opBoolean","MERGE",FACE,{"derivedFrom":[makeQuery(id+"F1.opExtrude","CAP_FACE",FACE,{"disambiguationData":[OSD([subQ8,subQ2,subQ7,subQ1,subQ6,subQ5,subQ4])],"isStart":false}),makeQuery(id+"F6.opExtrude","CAP_FACE",FACE,{"disambiguationData":[OSD([subQ3,sQuery(id+"F5.wireOp",EDGE,"E20"),sQuery(id+"F5.wireOp",EDGE,"E21.0"),subQ0])],"isStart":true}),makeQuery(id+"F6.opExtrude","CAP_FACE",FACE,{"disambiguationData":[OSD([subQ2,subQ1,subQ0,sQuery(id+"F5.wireOp",EDGE,"E23.0"),sQuery(id+"F5.wireOp",EDGE,"E25"),sQuery(id+"F5.wireOp",EDGE,"E26"),sQuery(id+"F5.wireOp",EDGE,"E27"),sQuery(id+"F5.wireOp",EDGE,"E28")])],"isStart":true})]}),makeQuery(id+"F8.opExtrude","CAP_FACE",FACE,{"disambiguationData":[OSD([sQuery(id+"F7.wireOp",EDGE,"E30.bottom"),sQuery(id+"F7.wireOp",EDGE,"E30.top"),sQuery(id+"F7.wireOp",EDGE,"E30.left"),sQuery(id+"F7.wireOp",EDGE,"E30.right")])],"isStart":true}),makeQuery(id+"F8.opExtrude","CAP_FACE",FACE,{"disambiguationData":[OSD([sQuery(id+"F7.wireOp",EDGE,"E31.bottom"),sQuery(id+"F7.wireOp",EDGE,"E31.top"),sQuery(id+"F7.wireOp",EDGE,"E31.left"),sQuery(id+"F7.wireOp",EDGE,"E31.right")])],"isStart":true}),makeQuery(id+"F8.opExtrude","CAP_FACE",FACE,{"disambiguationData":[OSD([sQuery(id+"F7.wireOp",EDGE,"E33.bottom"),sQuery(id+"F7.wireOp",EDGE,"E33.top"),sQuery(id+"F7.wireOp",EDGE,"E33.left"),sQuery(id+"F7.wireOp",EDGE,"E33.right")])],"isStart":true})]})],"blendedInto":[makeQuery(id+"F8.boolean.opBoolean","MERGE",FACE,{"derivedFrom":[makeQuery(id+"F6.boolean.opBoolean","MERGE",FACE,{"derivedFrom":[makeQuery(id+"F1.opExtrude","CAP_FACE",FACE,{"disambiguationData":[OSD([subQ8,subQ2,subQ7,subQ1,subQ6,subQ5,subQ4])],"isStart":false}),makeQuery(id+"F6.opExtrude","CAP_FACE",FACE,{"disambiguationData":[OSD([subQ3,sQuery(id+"F5.wireOp",EDGE,"E20"),sQuery(id+"F5.wireOp",EDGE,"E21.0"),subQ0])],"isStart":true}),makeQuery(id+"F6.opExtrude","CAP_FACE",FACE,{"disambiguationData":[OSD([subQ2,subQ1,subQ0,sQuery(id+"F5.wireOp",EDGE,"E23.0"),sQuery(id+"F5.wireOp",EDGE,"E25"),sQuery(id+"F5.wireOp",EDGE,"E26"),sQuery(id+"F5.wireOp",EDGE,"E27"),sQuery(id+"F5.wireOp",EDGE,"E28")])],"isStart":true})]}),makeQuery(id+"F8.opExtrude","CAP_FACE",FACE,{"disambiguationData":[OSD([sQuery(id+"F7.wireOp",EDGE,"E30.bottom"),sQuery(id+"F7.wireOp",EDGE,"E30.top"),sQuery(id+"F7.wireOp",EDGE,"E30.left"),sQuery(id+"F7.wireOp",EDGE,"E30.right")])],"isStart":true}),makeQuery(id+"F8.opExtrude","CAP_FACE",FACE,{"disambiguationData":[OSD([sQuery(id+"F7.wireOp",EDGE,"E31.bottom"),sQuery(id+"F7.wireOp",EDGE,"E31.top"),sQuery(id+"F7.wireOp",EDGE,"E31.left"),sQuery(id+"F7.wireOp",EDGE,"E31.right")])],"isStart":true}),makeQuery(id+"F8.opExtrude","CAP_FACE",FACE,{"disambiguationData":[OSD([sQuery(id+"F7.wireOp",EDGE,"E33.bottom"),sQuery(id+"F7.wireOp",EDGE,"E33.top"),sQuery(id+"F7.wireOp",EDGE,"E33.left"),sQuery(id+"F7.wireOp",EDGE,"E33.right")])],"isStart":true})]})]});}
            var Q2;
            {var subQ0=sQuery(id+"F5.wireOp",EDGE,"E20");var subQ4=sQuery(id+"F0.wireOp",EDGE,"E3");var subQ7=makeQuery(id+"F3.opShell","OFFSET_EDGE",EDGE,{"disambiguationData":[OSD([subQ4])]});Q2=makeQuery(id+"F6.boolean.opBoolean","SPLIT",EDGE,{"disambiguationData":[TD([makeQuery(id+"F6.opExtrude","SWEPT_FACE",FACE,{"disambiguationData":[OSD([subQ0])]})])],"derivedFrom":subQ7});}
            var Q3;
            Q3=makeQuery(id+"F2.boolean.opBoolean","COPY",EDGE,{"derivedFrom":makeQuery(id+"F2.opExtrude","CAP_EDGE",EDGE,{"disambiguationData":[OSD([sQuery(id+"F0.wireOp",EDGE,"E3")])],"isStart":false})});
            var Q4;
            Q4=makeQuery(id+"F8.boolean.opBoolean","MERGE",EDGE,{"derivedFrom":[makeQuery(id+"F1.opExtrude","CAP_EDGE",EDGE,{"disambiguationData":[OSD([sQuery(id+"F0.wireOp",EDGE,"E6")])],"isStart":false}),makeQuery(id+"F8.opExtrude","CAP_EDGE",EDGE,{"disambiguationData":[OSD([sQuery(id+"F7.wireOp",EDGE,"E30.left")])],"isStart":true})]});
            var Q5;
            {var subQ2=sQuery(id+"F0.wireOp",EDGE,"E7");var subQ3=sQuery(id+"F7.wireOp",EDGE,"E30.right");Q5=makeQuery(id+"F8.boolean.opBoolean","SPLIT",EDGE,{"disambiguationData":[TD([makeQuery(id+"F8.opExtrude","SWEPT_FACE",FACE,{"disambiguationData":[OSD([subQ3])]})])],"derivedFrom":makeQuery(id+"F1.opExtrude","CAP_EDGE",EDGE,{"disambiguationData":[OSD([subQ2])],"isStart":false})});}
            var Q6;
            {var subQ2=sQuery(id+"F0.wireOp",EDGE,"E7");var subQ3=sQuery(id+"F7.wireOp",EDGE,"E31.right");Q6=makeQuery(id+"F8.boolean.opBoolean","SPLIT",EDGE,{"disambiguationData":[TD([makeQuery(id+"F8.opExtrude","SWEPT_FACE",FACE,{"disambiguationData":[OSD([subQ3])]})])],"derivedFrom":makeQuery(id+"F1.opExtrude","CAP_EDGE",EDGE,{"disambiguationData":[OSD([subQ2])],"isStart":false})});}
            var Q7;
            {var subQ0=sQuery(id+"F5.wireOp",EDGE,"E26");Q7=makeQuery(id+"F6.opExtrude","CAP_EDGE",EDGE,{"disambiguationData":[OSD([subQ0]),TDD([makeQuery(id+"F5.imprint","IMPRINT",EDGE,{"disambiguationData":[TD([[makeQuery(id+"F5.imprint","INTERSECT",VERTEX,{"derivedFrom":[subQ0,sQuery(id+"F5.wireOp",EDGE,"E28")]}),-1.0]])],"derivedFrom":subQ0}),makeQuery(id+"F5.imprint","IMPRINT",EDGE,{"disambiguationData":[TD([[makeQuery(id+"F5.imprint","INTERSECT",VERTEX,{"derivedFrom":[sQuery(id+"F5.wireOp",EDGE,"E22.0"),subQ0]}),1.0]])],"derivedFrom":subQ0})])],"isStart":true});}
            var Q8;
            {var subQ1=sQuery(id+"F0.wireOp",EDGE,"E12");var subQ4=makeQuery(id+"F3.opShell","OFFSET_EDGE",EDGE,{"disambiguationData":[OSD([subQ1]),TDD([makeQuery(id+"F1.opExtrude","CAP_EDGE",EDGE,{"disambiguationData":[OSD([subQ1])],"isStart":false})])]});Q8=makeQuery(id+"F6.boolean.opBoolean","SPLIT",EDGE,{"disambiguationData":[TD([makeQuery(id+"F3.opShell","OFFSET_FACE",FACE,{"disambiguationData":[OSD([sQuery(id+"F0.wireOp",EDGE,"E4")])]})])],"derivedFrom":subQ4});}
            var Q9;
            Q9=makeQuery(id+"F2.boolean.opBoolean","COPY",EDGE,{"derivedFrom":makeQuery(id+"F2.opExtrude","CAP_EDGE",EDGE,{"disambiguationData":[OSD([sQuery(id+"F0.wireOp",EDGE,"E4")])],"isStart":false})});
            var Q10;
            {var subQ3=sQuery(id+"F0.wireOp",EDGE,"E4");var subQ4=makeQuery(id+"F3.opShell","OFFSET_EDGE",EDGE,{"disambiguationData":[OSD([subQ3])]});var subQ7=sQuery(id+"F0.wireOp",EDGE,"E8");Q10=makeQuery(id+"F6.boolean.opBoolean","SPLIT",EDGE,{"disambiguationData":[TD([makeQuery(id+"F3.opShell","OFFSET_FACE",FACE,{"disambiguationData":[OSD([subQ7])]})])],"derivedFrom":subQ4});}
            fillet(context, id + "F11", {"entities" : qUnion([Q0, Q1, Q2, Q3, Q4, Q5, Q6, Q7, Q8, Q9, Q10]), "radius" : 3 * mm, "tangentPropagation" : true, "allowEdgeOverflow" : false});
        }
        {
            var Q0;
            Q0=qCreatedBy(makeId("Front.planeOp"),FACE);
            cPlane(context, id + "F12", {"entities" : qUnion([Q0]), "cplaneType" : CPlaneType.OFFSET, "offset" : 40 * mm, "oppositeDirection" : true, "width" : 150 * mm, "height" : 150 * mm});
        }
        {
            var Q0;
            Q0=makeQuery(id+"F1.opExtrude","SWEPT_BODY",BODY,{"disambiguationData":[OSD([sQuery(id+"F0.wireOp",EDGE,"E6"),sQuery(id+"F0.wireOp",EDGE,"E7"),sQuery(id+"F0.wireOp",EDGE,"E8"),sQuery(id+"F0.wireOp",EDGE,"E12"),sQuery(id+"F0.wireOp",EDGE,"E13"),sQuery(id+"F0.wireOp",EDGE,"E14"),sQuery(id+"F0.wireOp",EDGE,"E15")])]});
            var Q1;
            Q1=qCreatedBy(id+"F12.planeOp",FACE);
            mirror(context, id + "F13", {"entities" : qUnion([Q0]), "mirrorPlane" : qUnion([Q1])});
        }
        {
            var Q0;
            Q0=qCreatedBy(id+"F12.planeOp",FACE);
            var sketch = newSketch(context, id + "F14", { "sketchPlane" : qUnion([Q0])});
            skLineSegment(sketch, "E34.0.0", {"start": v(-92.5, -66.45) * mm, "end": v(-92.5, -128.13) * mm});
            skLineSegment(sketch, "E34.0.1", {"start": v(-92.5, -128.13) * mm, "end": v(-82.5, -128.13) * mm});
            skLineSegment(sketch, "E34.0.2", {"start": v(-82.5, -128.13) * mm, "end": v(-82.5, -119) * mm});
            skArc(sketch, "E34.0.3", {"start": v(-82.5, -119) * mm, "mid": v(-81.33, -116.17) * mm, "end": v(-78.5, -115) * mm});
            skLineSegment(sketch, "E34.0.4", {"start": v(-78.5, -115) * mm, "end": v(-9, -115) * mm});
            skArc(sketch, "E34.0.5", {"start": v(-9, -115) * mm, "mid": v(-6.17, -116.17) * mm, "end": v(-5, -119) * mm});
            skLineSegment(sketch, "E34.0.6", {"start": v(-5, -119) * mm, "end": v(-5, -128.13) * mm});
            skLineSegment(sketch, "E34.0.7", {"start": v(-5, -128.13) * mm, "end": v(5, -128.13) * mm});
            skLineSegment(sketch, "E34.0.8", {"start": v(5, -128.13) * mm, "end": v(5, -119) * mm});
            skArc(sketch, "E34.0.9", {"start": v(5, -119) * mm, "mid": v(6.17, -116.17) * mm, "end": v(9, -115) * mm});
            skLineSegment(sketch, "E34.0.10", {"start": v(9, -115) * mm, "end": v(78.5, -115) * mm});
            skArc(sketch, "E34.0.11", {"start": v(78.5, -115) * mm, "mid": v(81.33, -116.17) * mm, "end": v(82.5, -119) * mm});
            skLineSegment(sketch, "E34.0.12", {"start": v(82.5, -119) * mm, "end": v(82.5, -128.13) * mm});
            skLineSegment(sketch, "E34.0.13", {"start": v(82.5, -128.13) * mm, "end": v(92.5, -128.13) * mm});
            skLineSegment(sketch, "E34.0.14", {"start": v(92.5, -128.13) * mm, "end": v(92.5, -66.45) * mm});
            skCircle(sketch, "E35.0", {"center": v(-80, -66.45) * mm, "radius": 7.5 * mm, "construction": true});
            skCircle(sketch, "E36.0", {"center": v(-40, -96) * mm, "radius": 7.5 * mm, "construction": true});
            skCircle(sketch, "E37.0", {"center": v(80, -66.45) * mm, "radius": 7.5 * mm, "construction": true});
            skCircle(sketch, "E38", {"center": v(-80, -66.45) * mm, "radius": 6.25 * mm});
            skCircle(sketch, "E39", {"center": v(-40, -96) * mm, "radius": 6.25 * mm});
            skCircle(sketch, "E40", {"center": v(80, -66.45) * mm, "radius": 6.25 * mm});
            skCircle(sketch, "E41", {"center": v(-80, -66.45) * mm, "radius": 12.5 * mm});
            skCircle(sketch, "E42", {"center": v(-40, -96) * mm, "radius": 12.5 * mm});
            skCircle(sketch, "E43", {"center": v(80, -66.45) * mm, "radius": 12.5 * mm});
            skLineSegment(sketch, "E44", {"start": v(-69.95, -73.88) * mm, "end": v(-50.05, -88.57) * mm});
            skLineSegment(sketch, "E45", {"start": v(-27.86, -93.01) * mm, "end": v(67.86, -69.44) * mm});
            skLineSegment(sketch, "E46", {"start": v(-82.5, -77.04) * mm, "end": v(-82.5, -105) * mm});
            skLineSegment(sketch, "E47", {"start": v(-82.5, -105) * mm, "end": v(-44.65, -105) * mm});
            skLineSegment(sketch, "E48", {"start": v(-44.65, -105) * mm, "end": v(-82.5, -77.04) * mm});
            skLineSegment(sketch, "E49", {"start": v(-34.73, -105) * mm, "end": v(82.5, -76.14) * mm});
            skLineSegment(sketch, "E50", {"start": v(82.5, -76.14) * mm, "end": v(82.5, -105) * mm});
            skLineSegment(sketch, "E51", {"start": v(82.5, -105) * mm, "end": v(-34.73, -105) * mm});
            skLineSegment(sketch, "E52", {"start": v(-92.5, -92.26) * mm, "end": v(-82.5, -92.26) * mm, "construction": true});
            skLineSegment(sketch, "E53", {"start": v(-63.57, -91.02) * mm, "end": v(-57.63, -82.98) * mm, "construction": true});
            skLineSegment(sketch, "E54", {"start": v(-63.57, -105) * mm, "end": v(-63.57, -115) * mm, "construction": true});
            skLineSegment(sketch, "E55", {"start": v(23.89, -90.57) * mm, "end": v(21.5, -80.86) * mm, "construction": true});
            skLineSegment(sketch, "E56", {"start": v(82.5, -90.57) * mm, "end": v(92.5, -90.57) * mm, "construction": true});
            skLineSegment(sketch, "E57", {"start": v(38.3, -105) * mm, "end": v(38.3, -115) * mm, "construction": true});
            skLineSegment(sketch, "E58", {"start": v(23.89, -90.57) * mm, "end": v(27.44, -105) * mm});
            skLineSegment(sketch, "E59", {"start": v(33.6, -88.18) * mm, "end": v(37.74, -105) * mm});
            skLineSegment(sketch, "E60", {"start": v(25.66, -97.78) * mm, "end": v(35.37, -95.4) * mm, "construction": true});
            skLineSegment(sketch, "E61", {"start": v(-69.95, -73.88) * mm, "end": v(67.86, -69.44) * mm});
            skLineSegment(sketch, "E62", {"start": v(-67.78, -63.8) * mm, "end": v(69.7, -59.38) * mm});
            skLineSegment(sketch, "E63", {"start": v(-8.33, -71.9) * mm, "end": v(-8.65, -61.9) * mm, "construction": true});
            skLineSegment(sketch, "E64", {"start": v(-27.86, -93.01) * mm, "end": v(-1.04, -71.66) * mm});
            skLineSegment(sketch, "E65", {"start": v(-15.2, -72.12) * mm, "end": v(-32.57, -85.94) * mm});
            skLineSegment(sketch, "E66", {"start": v(-14.45, -82.34) * mm, "end": v(-23.89, -79.03) * mm, "construction": true});
            skSolve(sketch);
        }
        {
            var Q0;
            Q0 = qSketchRegion(id + "F14", true);
            var Q1;
            {var subQ0=sQuery(id+"F14.wireOp",EDGE,"E58");Q1=makeQuery(id+"F14.imprint","IMPRINT",FACE,{"disambiguationData":[TD([[makeQuery(id+"F14.imprint","IMPRINT",EDGE,{"derivedFrom":subQ0}),1.0]])]});}
            var Q2;
            {var subQ0=sQuery(id+"F14.wireOp",EDGE,"E44");Q2=makeQuery(id+"F14.imprint","IMPRINT",FACE,{"disambiguationData":[TD([[makeQuery(id+"F14.imprint","IMPRINT",EDGE,{"derivedFrom":subQ0}),-1.0]])]});}
            var Q3;
            {var subQ0=sQuery(id+"F14.wireOp",EDGE,"E64");Q3=makeQuery(id+"F14.imprint","IMPRINT",FACE,{"disambiguationData":[TD([[makeQuery(id+"F14.imprint","IMPRINT",EDGE,{"derivedFrom":subQ0}),1.0]])]});}
            var Q4;
            {var subQ4=sQuery(id+"F14.wireOp",EDGE,"E45");Q4=makeQuery(id+"F14.imprint","IMPRINT",FACE,{"disambiguationData":[TD([[makeQuery(id+"F14.imprint","IMPRINT",EDGE,{"derivedFrom":subQ4}),-1.0]])]});}
            var Q5;
            Q5=makeQuery(id+"F14.imprint","IMPRINT",FACE,{"disambiguationData":[TD([[makeQuery(id+"F14.imprint","IMPRINT",EDGE,{"derivedFrom":sQuery(id+"F14.wireOp",EDGE,"E39")}),-1.0]])]});
            extrude(context, id + "F15", {"entities" : qUnion([Q0, Q1, Q2, Q3, Q4, Q5]), "depth" : 5 * mm, "offsetDistance" : 25 * mm});
        }
        {
            var Q0;
            Q0=makeQuery(id+"F15.opExtrude","SWEPT_EDGE",EDGE,{"disambiguationData":[OSD([sQuery(id+"F14.wireOp",EDGE,"E47"),sQuery(id+"F14.wireOp",EDGE,"E48")])]});
            var Q1;
            Q1=makeQuery(id+"F15.opExtrude","SWEPT_EDGE",EDGE,{"disambiguationData":[OSD([sQuery(id+"F14.wireOp",EDGE,"E46"),sQuery(id+"F14.wireOp",EDGE,"E47")])]});
            var Q2;
            Q2=makeQuery(id+"F15.opExtrude","SWEPT_EDGE",EDGE,{"disambiguationData":[OSD([sQuery(id+"F14.wireOp",EDGE,"E46"),sQuery(id+"F14.wireOp",EDGE,"E48")])]});
            var Q3;
            Q3=makeQuery(id+"F15.opExtrude","SWEPT_EDGE",EDGE,{"disambiguationData":[OSD([sQuery(id+"F14.wireOp",EDGE,"E41"),sQuery(id+"F14.wireOp",EDGE,"E44")])]});
            var Q4;
            Q4=makeQuery(id+"F15.opExtrude","SWEPT_EDGE",EDGE,{"disambiguationData":[OSD([sQuery(id+"F14.wireOp",EDGE,"E42"),sQuery(id+"F14.wireOp",EDGE,"E44")])]});
            var Q5;
            Q5=makeQuery(id+"F15.opExtrude","SWEPT_EDGE",EDGE,{"disambiguationData":[OSD([sQuery(id+"F14.wireOp",EDGE,"E42"),sQuery(id+"F14.wireOp",EDGE,"E45")])]});
            var Q6;
            Q6=makeQuery(id+"F15.opExtrude","SWEPT_EDGE",EDGE,{"disambiguationData":[OSD([sQuery(id+"F14.wireOp",EDGE,"E43"),sQuery(id+"F14.wireOp",EDGE,"E45")])]});
            var Q7;
            Q7=makeQuery(id+"F15.opExtrude","SWEPT_EDGE",EDGE,{"disambiguationData":[OSD([sQuery(id+"F14.wireOp",EDGE,"E50"),sQuery(id+"F14.wireOp",EDGE,"E51")])]});
            var Q8;
            Q8=makeQuery(id+"F15.opExtrude","SWEPT_EDGE",EDGE,{"disambiguationData":[OSD([sQuery(id+"F14.wireOp",EDGE,"E49"),sQuery(id+"F14.wireOp",EDGE,"E50")])]});
            var Q9;
            Q9=makeQuery(id+"F15.opExtrude","SWEPT_EDGE",EDGE,{"disambiguationData":[OSD([sQuery(id+"F14.wireOp",EDGE,"E49"),sQuery(id+"F14.wireOp",EDGE,"E51")])]});
            var Q10;
            Q10=makeQuery(id+"F15.opExtrude","SWEPT_EDGE",EDGE,{"disambiguationData":[OSD([sQuery(id+"F14.wireOp",EDGE,"E49"),sQuery(id+"F14.wireOp",EDGE,"E58")])]});
            var Q11;
            Q11=makeQuery(id+"F15.opExtrude","SWEPT_EDGE",EDGE,{"disambiguationData":[OSD([sQuery(id+"F14.wireOp",EDGE,"E51"),sQuery(id+"F14.wireOp",EDGE,"E58")])]});
            var Q12;
            Q12=makeQuery(id+"F15.opExtrude","SWEPT_EDGE",EDGE,{"disambiguationData":[OSD([sQuery(id+"F14.wireOp",EDGE,"E49"),sQuery(id+"F14.wireOp",EDGE,"E59")])]});
            var Q13;
            Q13=makeQuery(id+"F15.opExtrude","SWEPT_EDGE",EDGE,{"disambiguationData":[OSD([sQuery(id+"F14.wireOp",EDGE,"E51"),sQuery(id+"F14.wireOp",EDGE,"E59")])]});
            var Q14;
            Q14=makeQuery(id+"F15.opExtrude","SWEPT_EDGE",EDGE,{"disambiguationData":[OSD([sQuery(id+"F14.wireOp",EDGE,"E61"),sQuery(id+"F14.wireOp",EDGE,"E64")])]});
            var Q15;
            Q15=makeQuery(id+"F15.opExtrude","SWEPT_EDGE",EDGE,{"disambiguationData":[OSD([sQuery(id+"F14.wireOp",EDGE,"E61"),sQuery(id+"F14.wireOp",EDGE,"E65")])]});
            var Q16;
            Q16=makeQuery(id+"F15.opExtrude","SWEPT_EDGE",EDGE,{"disambiguationData":[OSD([sQuery(id+"F14.wireOp",EDGE,"E42"),sQuery(id+"F14.wireOp",EDGE,"E65")])]});
            fillet(context, id + "F16", {"entities" : qUnion([Q0, Q1, Q2, Q3, Q4, Q5, Q6, Q7, Q8, Q9, Q10, Q11, Q12, Q13, Q14, Q15, Q16]), "radius" : 4 * mm, "tangentPropagation" : true, "allowEdgeOverflow" : false});
        }
        {
            var Q0;
            Q0=makeQuery(id+"F15.opExtrude","SWEPT_FACE",FACE,{"disambiguationData":[OSD([sQuery(id+"F14.wireOp",EDGE,"E46")])]});
            var Q1;
            Q1=makeQuery(id+"F15.opExtrude","SWEPT_FACE",FACE,{"disambiguationData":[OSD([sQuery(id+"F14.wireOp",EDGE,"E44")])]});
            var Q2;
            Q2=makeQuery(id+"F15.opExtrude","SWEPT_FACE",FACE,{"disambiguationData":[OSD([sQuery(id+"F14.wireOp",EDGE,"E45")])]});
            var Q3;
            {var subQ0=sQuery(id+"F14.wireOp",EDGE,"E51");Q3=makeQuery(id+"F15.opExtrude","SWEPT_FACE",FACE,{"disambiguationData":[OSD([subQ0]),TDD([makeQuery(id+"F14.imprint","IMPRINT",EDGE,{"disambiguationData":[TD([[makeQuery(id+"F14.imprint","INTERSECT",VERTEX,{"derivedFrom":[subQ0,sQuery(id+"F14.wireOp",EDGE,"E58")]}),-1.0]])],"derivedFrom":subQ0}),makeQuery(id+"F14.imprint","IMPRINT",EDGE,{"disambiguationData":[TD([[makeQuery(id+"F14.imprint","INTERSECT",VERTEX,{"derivedFrom":[sQuery(id+"F14.wireOp",EDGE,"E49"),subQ0]}),1.0]])],"derivedFrom":subQ0})])]});}
            var Q4;
            {var subQ0=sQuery(id+"F14.wireOp",EDGE,"E51");Q4=makeQuery(id+"F15.opExtrude","SWEPT_FACE",FACE,{"disambiguationData":[OSD([subQ0]),TDD([makeQuery(id+"F14.imprint","IMPRINT",EDGE,{"disambiguationData":[TD([[makeQuery(id+"F14.imprint","INTERSECT",VERTEX,{"derivedFrom":[sQuery(id+"F14.wireOp",EDGE,"E50"),subQ0]}),-1.0]])],"derivedFrom":subQ0})])]});}
            var Q5;
            Q5=makeQuery(id+"F15.opExtrude","SWEPT_FACE",FACE,{"disambiguationData":[OSD([sQuery(id+"F14.wireOp",EDGE,"E62")])]});
            var Q6;
            Q6=makeQuery(id+"F15.opExtrude","SWEPT_FACE",FACE,{"disambiguationData":[OSD([sQuery(id+"F14.wireOp",EDGE,"E34.0.4")])]});
            var Q7;
            Q7=makeQuery(id+"F15.opExtrude","SWEPT_FACE",FACE,{"disambiguationData":[OSD([sQuery(id+"F14.wireOp",EDGE,"E34.0.10")])]});
            fillet(context, id + "F17", {"entities" : qUnion([Q0, Q1, Q2, Q3, Q4, Q5, Q6, Q7]), "radius" : 1 * mm, "tangentPropagation" : true, "allowEdgeOverflow" : false});
        }
        {
            var Q0;
            Q0=qCreatedBy(makeId("Front.planeOp"),FACE);
            var sketch = newSketch(context, id + "F18", { "sketchPlane" : qUnion([Q0])});
            skCircle(sketch, "E67", {"center": v(-93.97, 67.54) * mm, "radius": 15 * mm});
            skCircle(sketch, "E68", {"center": v(-93.97, 67.54) * mm, "radius": 4.25 * mm});
            skCircle(sketch, "E69", {"center": v(-54.3, 71.82) * mm, "radius": 4 * mm});
            skCircle(sketch, "E70", {"center": v(-54.3, 71.82) * mm, "radius": 10 * mm});
            skSolve(sketch);
        }
        {
            var Q0;
            Q0=makeQuery(id+"F18.imprint","IMPRINT",FACE,{"disambiguationData":[TD([[makeQuery(id+"F18.imprint","IMPRINT",EDGE,{"derivedFrom":sQuery(id+"F18.wireOp",EDGE,"E67")}),1.0]])]});
            extrude(context, id + "F19", {"entities" : qUnion([Q0]), "depth" : 1 * mm, "offsetDistance" : 25 * mm});
        }
        {
            var Q0;
            Q0=makeQuery(id+"F18.imprint","IMPRINT",FACE,{"disambiguationData":[TD([[makeQuery(id+"F18.imprint","IMPRINT",EDGE,{"derivedFrom":sQuery(id+"F18.wireOp",EDGE,"E69")}),-1.0]])]});
            extrude(context, id + "F20", {"entities" : qUnion([Q0]), "depth" : 4 * mm, "offsetDistance" : 25 * mm});
        }
        {
            var Q0;
            Q0=makeQuery(id+"F20.opExtrude","CAP_EDGE",EDGE,{"disambiguationData":[OSD([sQuery(id+"F18.wireOp",EDGE,"E70")])],"isStart":false});
            var Q1;
            Q1=makeQuery(id+"F20.opExtrude","CAP_FACE",FACE,{"disambiguationData":[OSD([sQuery(id+"F18.wireOp",EDGE,"E69"),sQuery(id+"F18.wireOp",EDGE,"E70")])],"isStart":true});
            fillet(context, id + "F21", {"entities" : qUnion([Q0, Q1]), "radius" : 1 * mm, "tangentPropagation" : true, "allowEdgeOverflow" : false});
        }
        {
            var Q0;
            Q0=makeQuery(id+"F19.opExtrude","CAP_FACE",FACE,{"disambiguationData":[OSD([sQuery(id+"F18.wireOp",EDGE,"E67"),sQuery(id+"F18.wireOp",EDGE,"E68")])],"isStart":true});
            var Q1;
            Q1=makeQuery(id+"F19.opExtrude","CAP_FACE",FACE,{"disambiguationData":[OSD([sQuery(id+"F18.wireOp",EDGE,"E67"),sQuery(id+"F18.wireOp",EDGE,"E68")])],"isStart":false});
            fillet(context, id + "F22", {"entities" : qUnion([Q0, Q1]), "radius" : 0.5 * mm, "tangentPropagation" : true, "allowEdgeOverflow" : false});
        }
    });
